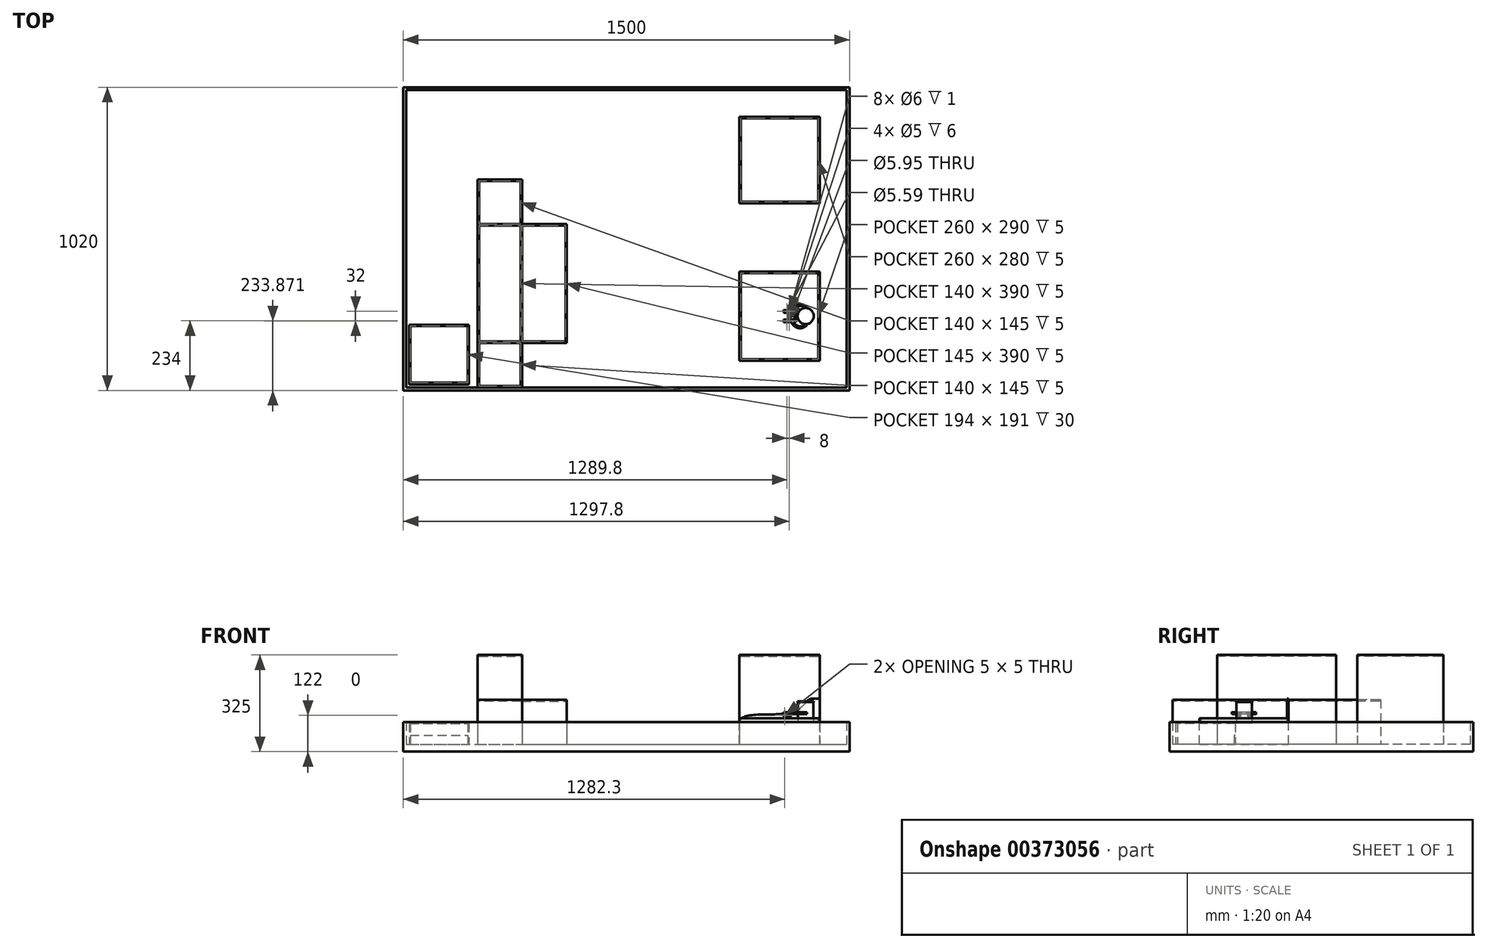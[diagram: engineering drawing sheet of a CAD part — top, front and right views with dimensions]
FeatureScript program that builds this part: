
annotation { "Feature Type Name" : "Feature", "Feature Type Description" : "" }
export const myFeature = defineFeature(function(context is Context, id is Id, definition is map)
    precondition{}
    {
        {
            var Q0;
            Q0=qCreatedBy(makeId("Top.planeOp"),FACE);
            var sketch = newSketch(context, id + "F0", { "sketchPlane" : qUnion([Q0])});
            skCircle(sketch, "E0", {"center": v(0, 0) * mm, "radius": 27.2 * mm});
            skSolve(sketch);
        }
        {
            var Q0;
            Q0=qSketchRegion(id+"F0",true);
            extrude(context, id + "F1", {"entities" : qUnion([Q0]), "depth" : 2.83 * mm});
        }
        {
            var Q0;
            Q0=makeQuery(id+"F1.opExtrude","CAP_FACE",FACE,{"disambiguationData":[OSD([sQuery(id+"F0.wireOp",EDGE,"E0")])],"isStart":false});
            var sketch = newSketch(context, id + "F2", { "sketchPlane" : qUnion([Q0])});
            skCircle(sketch, "E1", {"center": v(0, 0) * mm, "radius": 26.4 * mm});
            skSolve(sketch);
        }
        {
            var Q0;
            Q0=qSketchRegion(id+"F2",true);
            extrude(context, id + "F3", {"entities" : qUnion([Q0]), "operationType" : NewBodyOperationType.ADD, "depth" : 67.36 * mm});
        }
        {
            var Q0;
            Q0=makeQuery(id+"F3.opExtrude","CAP_FACE",FACE,{"disambiguationData":[OSD([sQuery(id+"F2.wireOp",EDGE,"E1")])],"isStart":false});
            var sketch = newSketch(context, id + "F4", { "sketchPlane" : qUnion([Q0])});
            skCircle(sketch, "E2", {"center": v(0, 0) * mm, "radius": 27.2 * mm});
            skSolve(sketch);
        }
        {
            var Q0;
            Q0=qSketchRegion(id+"F4",true);
            extrude(context, id + "F5", {"entities" : qUnion([Q0]), "operationType" : NewBodyOperationType.ADD, "depth" : 2.83 * mm});
        }
        {
            var Q0;
            Q0=makeQuery(id+"F5.opExtrude","CAP_FACE",FACE,{"disambiguationData":[OSD([sQuery(id+"F4.wireOp",EDGE,"E2")])],"isStart":false});
            var sketch = newSketch(context, id + "F6", { "sketchPlane" : qUnion([Q0])});
            skSolve(sketch);
        }
        {
            var Q0;
            Q0=qCreatedBy(makeId("Top.planeOp"),FACE);
            cPlane(context, id + "F7", {"entities" : qUnion([Q0]), "cplaneType" : CPlaneType.OFFSET, "offset" : 25 * mm, "width" : 150 * mm, "height" : 150 * mm});
        }
        {
            var Q0;
            Q0=makeQuery(id+"F6.imprint","IMPRINT",FACE,{"disambiguationData":[TD([[makeQuery(id+"F6.imprint","IMPRINT",EDGE,{"derivedFrom":makeQuery(id+"F5.opExtrude","CAP_EDGE",EDGE,{"disambiguationData":[OSD([sQuery(id+"F4.wireOp",EDGE,"E2")])],"isStart":false})}),1.0]])]});
            var sketch = newSketch(context, id + "F8", { "sketchPlane" : qUnion([Q0])});
            skSolve(sketch);
        }
        {
            var Q0;
            Q0=qCreatedBy(makeId("Top.planeOp"),FACE);
            var sketch = newSketch(context, id + "F9", { "sketchPlane" : qUnion([Q0])});
            skLineSegment(sketch, "E3.bottom", {"start": v(-222.8, -150) * mm, "end": v(47.2, -150) * mm});
            skLineSegment(sketch, "E3.top", {"start": v(-222.8, 150) * mm, "end": v(47.2, 150) * mm});
            skLineSegment(sketch, "E3.left", {"start": v(-222.8, -150) * mm, "end": v(-222.8, 150) * mm});
            skLineSegment(sketch, "E3.right", {"start": v(47.2, -150) * mm, "end": v(47.2, 150) * mm});
            skSolve(sketch);
        }
        {
            var Q0;
            Q0=qSketchRegion(id+"F9",true);
            extrude(context, id + "F10", {"entities" : qUnion([Q0]), "oppositeDirection" : true, "depth" : 72 * mm});
        }
        {
            var Q0;
            Q0=makeQuery(id+"F10.opExtrude","CAP_FACE",FACE,{"disambiguationData":[OSD([sQuery(id+"F9.wireOp",EDGE,"E3.bottom"),sQuery(id+"F9.wireOp",EDGE,"E3.top"),sQuery(id+"F9.wireOp",EDGE,"E3.left"),sQuery(id+"F9.wireOp",EDGE,"E3.right")])],"isStart":true});
            var sketch = newSketch(context, id + "F11", { "sketchPlane" : qUnion([Q0])});
            skLineSegment(sketch, "E4.bottom", {"start": v(-222.8, -150) * mm, "end": v(47.2, -150) * mm});
            skLineSegment(sketch, "E4.top", {"start": v(-222.8, -145) * mm, "end": v(42.2, -145) * mm});
            skLineSegment(sketch, "E4.left", {"start": v(-222.8, -150) * mm, "end": v(-222.8, -145) * mm});
            skLineSegment(sketch, "E5.bottom", {"start": v(47.2, 150) * mm, "end": v(42.2, 150) * mm});
            skLineSegment(sketch, "E5.left", {"start": v(47.2, 150) * mm, "end": v(47.2, -150) * mm});
            skLineSegment(sketch, "E5.right", {"start": v(42.2, 150) * mm, "end": v(42.2, -145) * mm});
            skSolve(sketch);
        }
        {
            var Q0;
            Q0=qSketchRegion(id+"F11",true);
            extrude(context, id + "F12", {"entities" : qUnion([Q0]), "operationType" : NewBodyOperationType.ADD, "depth" : 15 * mm});
        }
        {
            var Q0;
            Q0=makeQuery(id+"F12.boolean.opBoolean","MERGE",FACE,{"derivedFrom":[makeQuery(id+"F10.opExtrude","SWEPT_FACE",FACE,{"disambiguationData":[OSD([sQuery(id+"F9.wireOp",EDGE,"E3.top")])]}),makeQuery(id+"F12.opExtrude","SWEPT_FACE",FACE,{"disambiguationData":[OSD([sQuery(id+"F11.wireOp",EDGE,"E5.bottom")])]})]});
            var sketch = newSketch(context, id + "F13", { "sketchPlane" : qUnion([Q0])});
            skLineSegment(sketch, "E6", {"start": v(-47.2, 81.36) * mm, "end": v(-21.31, 81.36) * mm});
            skFitSpline(sketch, "E7", {"points": [v(-21.31, 81.36) * mm, v(15.24, 52.01) * mm, v(114.14, 28.17) * mm, v(222.8, 0) * mm], "startDerivative": vector(181.02, 0.3) * mm, "endDerivative": vector(-1.73, -239.85) * mm});
            skLineSegment(sketch, "E8", {"start": v(-47.2, 81.36) * mm, "end": v(-47.2, -72) * mm});
            skLineSegment(sketch, "E9", {"start": v(-47.2, -72) * mm, "end": v(222.8, -72) * mm});
            skLineSegment(sketch, "E10", {"start": v(222.8, -72) * mm, "end": v(222.8, 0) * mm});
            skSolve(sketch);
        }
        {
            var Q0;
            Q0=qSketchRegion(id+"F13",true);
            extrude(context, id + "F14", {"entities" : qUnion([Q0]), "operationType" : NewBodyOperationType.ADD, "oppositeDirection" : true, "depth" : 5 * mm});
        }
        {
            var Q0;
            Q0=makeQuery(id+"F10.opExtrude","CAP_FACE",FACE,{"disambiguationData":[OSD([sQuery(id+"F9.wireOp",EDGE,"E3.bottom"),sQuery(id+"F9.wireOp",EDGE,"E3.top"),sQuery(id+"F9.wireOp",EDGE,"E3.left"),sQuery(id+"F9.wireOp",EDGE,"E3.right")])],"isStart":true});
            var sketch = newSketch(context, id + "F15", { "sketchPlane" : qUnion([Q0])});
            skLineSegment(sketch, "E11.bottom", {"start": v(-222.8, 145) * mm, "end": v(-217.8, 145) * mm});
            skLineSegment(sketch, "E11.top", {"start": v(-222.8, -145) * mm, "end": v(-217.8, -145) * mm});
            skLineSegment(sketch, "E11.left", {"start": v(-222.8, 145) * mm, "end": v(-222.8, -145) * mm});
            skLineSegment(sketch, "E11.right", {"start": v(-217.8, 145) * mm, "end": v(-217.8, -145) * mm});
            skSolve(sketch);
        }
        {
            var Q0;
            Q0=qSketchRegion(id+"F15",true);
            extrude(context, id + "F16", {"entities" : qUnion([Q0]), "operationType" : NewBodyOperationType.ADD, "depth" : 5 * mm});
        }
        {
            var Q0;
            Q0=makeQuery(id+"F10.opExtrude","CAP_FACE",FACE,{"disambiguationData":[OSD([sQuery(id+"F9.wireOp",EDGE,"E3.bottom"),sQuery(id+"F9.wireOp",EDGE,"E3.top"),sQuery(id+"F9.wireOp",EDGE,"E3.left"),sQuery(id+"F9.wireOp",EDGE,"E3.right")])],"isStart":false});
            var sketch = newSketch(context, id + "F17", { "sketchPlane" : qUnion([Q0])});
            skLineSegment(sketch, "E12.bottom", {"start": v(147.2, 250) * mm, "end": v(-1352.8, 250) * mm});
            skLineSegment(sketch, "E12.top", {"start": v(147.2, -770) * mm, "end": v(-1352.8, -770) * mm});
            skLineSegment(sketch, "E12.left", {"start": v(147.2, 250) * mm, "end": v(147.2, -770) * mm});
            skLineSegment(sketch, "E12.right", {"start": v(-1352.8, 250) * mm, "end": v(-1352.8, -770) * mm});
            skSolve(sketch);
        }
        {
            var Q0;
            Q0=qSketchRegion(id+"F17",true);
            extrude(context, id + "F18", {"entities" : qUnion([Q0]), "operationType" : NewBodyOperationType.ADD, "depth" : 25 * mm});
        }
        {
            var Q0;
            Q0=makeQuery(id+"F18.opExtrude","CAP_FACE",FACE,{"disambiguationData":[OSD([sQuery(id+"F17.wireOp",EDGE,"E12.bottom"),sQuery(id+"F17.wireOp",EDGE,"E12.top"),sQuery(id+"F17.wireOp",EDGE,"E12.left"),sQuery(id+"F17.wireOp",EDGE,"E12.right")])],"isStart":true});
            var sketch = newSketch(context, id + "F19", { "sketchPlane" : qUnion([Q0])});
            skLineSegment(sketch, "E13.bottom", {"start": v(-222.8, 670) * mm, "end": v(47.2, 670) * mm});
            skLineSegment(sketch, "E13.top", {"start": v(-222.8, 380) * mm, "end": v(47.2, 380) * mm});
            skLineSegment(sketch, "E13.left", {"start": v(-222.8, 670) * mm, "end": v(-222.8, 380) * mm});
            skLineSegment(sketch, "E13.right", {"start": v(47.2, 670) * mm, "end": v(47.2, 380) * mm});
            skSolve(sketch);
        }
        {
            var Q0;
            Q0=qSketchRegion(id+"F19",true);
            extrude(context, id + "F20", {"entities" : qUnion([Q0]), "operationType" : NewBodyOperationType.ADD, "depth" : 300 * mm});
        }
        {
            var Q0;
            Q0=makeQuery(id+"F20.opExtrude","CAP_FACE",FACE,{"disambiguationData":[OSD([sQuery(id+"F19.wireOp",EDGE,"E13.bottom"),sQuery(id+"F19.wireOp",EDGE,"E13.top"),sQuery(id+"F19.wireOp",EDGE,"E13.left"),sQuery(id+"F19.wireOp",EDGE,"E13.right")])],"isStart":false});
            var sketch = newSketch(context, id + "F21", { "sketchPlane" : qUnion([Q0])});
            skLineSegment(sketch, "E14.bottom", {"start": v(-217.8, 665) * mm, "end": v(42.2, 665) * mm});
            skLineSegment(sketch, "E14.top", {"start": v(-217.8, 385) * mm, "end": v(42.2, 385) * mm});
            skLineSegment(sketch, "E14.left", {"start": v(-217.8, 665) * mm, "end": v(-217.8, 385) * mm});
            skLineSegment(sketch, "E14.right", {"start": v(42.2, 665) * mm, "end": v(42.2, 385) * mm});
            skSolve(sketch);
        }
        {
            var Q0;
            Q0=qSketchRegion(id+"F21",true);
            extrude(context, id + "F22", {"entities" : qUnion([Q0]), "operationType" : NewBodyOperationType.REMOVE, "oppositeDirection" : true, "depth" : 5 * mm});
        }
        {
            var Q0;
            Q0=makeQuery(id+"F18.opExtrude","CAP_FACE",FACE,{"disambiguationData":[OSD([sQuery(id+"F17.wireOp",EDGE,"E12.bottom"),sQuery(id+"F17.wireOp",EDGE,"E12.top"),sQuery(id+"F17.wireOp",EDGE,"E12.left"),sQuery(id+"F17.wireOp",EDGE,"E12.right")])],"isStart":true});
            var sketch = newSketch(context, id + "F23", { "sketchPlane" : qUnion([Q0])});
            skLineSegment(sketch, "E15.bottom", {"start": v(-1352.8, 770) * mm, "end": v(147.2, 770) * mm});
            skLineSegment(sketch, "E15.top", {"start": v(-1352.8, -250) * mm, "end": v(147.2, -250) * mm});
            skLineSegment(sketch, "E15.left", {"start": v(-1352.8, 770) * mm, "end": v(-1352.8, -250) * mm});
            skLineSegment(sketch, "E15.right", {"start": v(147.2, 770) * mm, "end": v(147.2, -250) * mm});
            skLineSegment(sketch, "E16.bottom", {"start": v(-1342.8, 760) * mm, "end": v(137.2, 760) * mm});
            skLineSegment(sketch, "E16.top", {"start": v(-1342.8, -240) * mm, "end": v(137.2, -240) * mm});
            skLineSegment(sketch, "E16.left", {"start": v(-1342.8, 760) * mm, "end": v(-1342.8, -240) * mm});
            skLineSegment(sketch, "E16.right", {"start": v(137.2, 760) * mm, "end": v(137.2, -240) * mm});
            skSolve(sketch);
        }
        {
            var Q0;
            Q0=qSketchRegion(id+"F23",true);
            extrude(context, id + "F24", {"entities" : qUnion([Q0]), "operationType" : NewBodyOperationType.ADD, "depth" : 75 * mm});
        }
        {
            var Q0;
            Q0=makeQuery(id+"F18.opExtrude","CAP_FACE",FACE,{"disambiguationData":[OSD([sQuery(id+"F17.wireOp",EDGE,"E12.bottom"),sQuery(id+"F17.wireOp",EDGE,"E12.top"),sQuery(id+"F17.wireOp",EDGE,"E12.left"),sQuery(id+"F17.wireOp",EDGE,"E12.right")])],"isStart":true});
            var sketch = newSketch(context, id + "F25", { "sketchPlane" : qUnion([Q0])});
            skLineSegment(sketch, "E17.bottom", {"start": v(-1102.8, 460) * mm, "end": v(-952.8, 460) * mm});
            skLineSegment(sketch, "E17.top", {"start": v(-1102.8, -240) * mm, "end": v(-952.8, -240) * mm});
            skLineSegment(sketch, "E17.left", {"start": v(-1102.8, 460) * mm, "end": v(-1102.8, -240) * mm});
            skLineSegment(sketch, "E17.right", {"start": v(-952.8, 460) * mm, "end": v(-952.8, 310) * mm});
            skLineSegment(sketch, "E18.bottom", {"start": v(-952.8, 310) * mm, "end": v(-802.8, 310) * mm});
            skLineSegment(sketch, "E18.top", {"start": v(-952.8, -90) * mm, "end": v(-802.8, -90) * mm});
            skLineSegment(sketch, "E18.right", {"start": v(-802.8, 310) * mm, "end": v(-802.8, -90) * mm});
            skLineSegment(sketch, "E19.trimOffspring", {"start": v(-952.8, -90) * mm, "end": v(-952.8, -240) * mm});
            skSolve(sketch);
        }
        {
            var Q0;
            Q0=qSketchRegion(id+"F25",true);
            extrude(context, id + "F26", {"entities" : qUnion([Q0]), "operationType" : NewBodyOperationType.ADD, "depth" : 150 * mm});
        }
        {
            var Q0;
            Q0=makeQuery(id+"F26.opExtrude","CAP_FACE",FACE,{"disambiguationData":[OSD([sQuery(id+"F25.wireOp",EDGE,"E17.bottom"),sQuery(id+"F25.wireOp",EDGE,"E17.top"),sQuery(id+"F25.wireOp",EDGE,"E17.left"),sQuery(id+"F25.wireOp",EDGE,"E17.right"),sQuery(id+"F25.wireOp",EDGE,"E18.bottom"),sQuery(id+"F25.wireOp",EDGE,"E18.top"),sQuery(id+"F25.wireOp",EDGE,"E18.right"),sQuery(id+"F25.wireOp",EDGE,"E19.trimOffspring")])],"isStart":false});
            var sketch = newSketch(context, id + "F27", { "sketchPlane" : qUnion([Q0])});
            skLineSegment(sketch, "E20.bottom", {"start": v(-952.8, 310) * mm, "end": v(-1102.8, 310) * mm});
            skLineSegment(sketch, "E20.top", {"start": v(-952.8, -90) * mm, "end": v(-1102.8, -90) * mm});
            skLineSegment(sketch, "E20.left", {"start": v(-952.8, 310) * mm, "end": v(-952.8, -90) * mm});
            skLineSegment(sketch, "E20.right", {"start": v(-1102.8, 310) * mm, "end": v(-1102.8, -90) * mm});
            skSolve(sketch);
        }
        {
            var Q0;
            Q0=qSketchRegion(id+"F27",true);
            extrude(context, id + "F28", {"entities" : qUnion([Q0]), "operationType" : NewBodyOperationType.ADD, "depth" : 150 * mm});
        }
        {
            var Q0;
            Q0=makeQuery(id+"F28.opExtrude","CAP_FACE",FACE,{"disambiguationData":[OSD([sQuery(id+"F27.wireOp",EDGE,"E20.bottom"),sQuery(id+"F27.wireOp",EDGE,"E20.top"),sQuery(id+"F27.wireOp",EDGE,"E20.left"),sQuery(id+"F27.wireOp",EDGE,"E20.right")])],"isStart":false});
            var sketch = newSketch(context, id + "F29", { "sketchPlane" : qUnion([Q0])});
            skLineSegment(sketch, "E21.bottom", {"start": v(-1097.8, 305) * mm, "end": v(-957.8, 305) * mm});
            skLineSegment(sketch, "E21.top", {"start": v(-1097.8, -85) * mm, "end": v(-957.8, -85) * mm});
            skLineSegment(sketch, "E21.left", {"start": v(-1097.8, 305) * mm, "end": v(-1097.8, -85) * mm});
            skLineSegment(sketch, "E21.right", {"start": v(-957.8, 305) * mm, "end": v(-957.8, -85) * mm});
            skSolve(sketch);
        }
        {
            var Q0;
            Q0=qSketchRegion(id+"F29",true);
            extrude(context, id + "F30", {"entities" : qUnion([Q0]), "operationType" : NewBodyOperationType.REMOVE, "oppositeDirection" : true, "depth" : 5 * mm});
        }
        {
            var Q0;
            {var subQ0=sQuery(id+"F25.wireOp",EDGE,"E17.left");var subQ1=sQuery(id+"F25.wireOp",EDGE,"E18.bottom");var subQ2=sQuery(id+"F25.wireOp",EDGE,"E17.right");var subQ3=sQuery(id+"F25.wireOp",EDGE,"E17.bottom");var subQ4=makeQuery(id+"F26.opExtrude","CAP_FACE",FACE,{"disambiguationData":[OSD([subQ3,sQuery(id+"F25.wireOp",EDGE,"E17.top"),subQ0,subQ2,subQ1,sQuery(id+"F25.wireOp",EDGE,"E18.top"),sQuery(id+"F25.wireOp",EDGE,"E18.right"),sQuery(id+"F25.wireOp",EDGE,"E19.trimOffspring")])],"isStart":false});Q0=makeQuery(id+"F28.boolean.opBoolean","SPLIT",FACE,{"disambiguationData":[TD([makeQuery(id+"F26.opExtrude","SWEPT_FACE",FACE,{"disambiguationData":[OSD([subQ3])]})])],"derivedFrom":subQ4});}
            var sketch = newSketch(context, id + "F31", { "sketchPlane" : qUnion([Q0])});
            skLineSegment(sketch, "E22.bottom", {"start": v(-1097.8, 455) * mm, "end": v(-957.8, 455) * mm});
            skLineSegment(sketch, "E22.top", {"start": v(-1097.8, 310) * mm, "end": v(-957.8, 310) * mm});
            skLineSegment(sketch, "E22.left", {"start": v(-1097.8, 455) * mm, "end": v(-1097.8, 310) * mm});
            skLineSegment(sketch, "E22.right", {"start": v(-957.8, 455) * mm, "end": v(-957.8, 310) * mm});
            skLineSegment(sketch, "E23.bottom", {"start": v(-952.8, 305) * mm, "end": v(-807.8, 305) * mm});
            skLineSegment(sketch, "E23.top", {"start": v(-952.8, -85) * mm, "end": v(-807.8, -85) * mm});
            skLineSegment(sketch, "E23.left", {"start": v(-952.8, 305) * mm, "end": v(-952.8, -85) * mm});
            skLineSegment(sketch, "E23.right", {"start": v(-807.8, 305) * mm, "end": v(-807.8, -85) * mm});
            skLineSegment(sketch, "E24.bottom", {"start": v(-1097.8, -90) * mm, "end": v(-957.8, -90) * mm});
            skLineSegment(sketch, "E24.top", {"start": v(-1097.8, -235) * mm, "end": v(-957.8, -235) * mm});
            skLineSegment(sketch, "E24.left", {"start": v(-1097.8, -90) * mm, "end": v(-1097.8, -235) * mm});
            skLineSegment(sketch, "E24.right", {"start": v(-957.8, -90) * mm, "end": v(-957.8, -235) * mm});
            skSolve(sketch);
        }
        {
            var Q0;
            Q0=qSketchRegion(id+"F31",true);
            extrude(context, id + "F32", {"entities" : qUnion([Q0]), "operationType" : NewBodyOperationType.REMOVE, "oppositeDirection" : true, "depth" : 5 * mm});
        }
        {
            var Q0;
            Q0=qCreatedBy(id+"F7.planeOp",FACE);
            var sketch = newSketch(context, id + "F33", { "sketchPlane" : qUnion([Q0])});
            skLineSegment(sketch, "E25", {"start": v(0, 0) * mm, "end": v(-90, 0) * mm, "construction": true});
            skLineSegment(sketch, "E26.bottom", {"start": v(-74.5, -12) * mm, "end": v(-55, -12) * mm});
            skLineSegment(sketch, "E26.top", {"start": v(-74.5, -20) * mm, "end": v(-55, -20) * mm});
            skLineSegment(sketch, "E26.left", {"start": v(-74.5, -12) * mm, "end": v(-74.5, -13) * mm});
            skPoint(sketch, "E27.visualSharp", {"position": v(-51, -12) * mm});
            skPoint(sketch, "E28.visualSharp", {"position": v(-51, -20) * mm});
            skCircle(sketch, "E29", {"center": v(-55, -16) * mm, "radius": 3 * mm});
            skLineSegment(sketch, "E30", {"start": v(-59, -3.98) * mm, "end": v(-59, -18.08) * mm, "construction": true});
            skCircle(sketch, "E31.MirrorC", {"center": v(-63, -16) * mm, "radius": 3 * mm});
            skLineSegment(sketch, "E32.bottom", {"start": v(-74.5, -13) * mm, "end": v(-65.65, -13) * mm});
            skLineSegment(sketch, "E32.top", {"start": v(-74.5, -19) * mm, "end": v(-65.65, -19) * mm});
            skArc(sketch, "E33", {"start": v(-65.65, -13) * mm, "mid": v(-67, -16) * mm, "end": v(-65.65, -19) * mm});
            skLineSegment(sketch, "E34.trimOffspring", {"start": v(-74.5, -19) * mm, "end": v(-74.5, -20) * mm});
            skArc(sketch, "E35.trimOffspring", {"start": v(-55, -20) * mm, "mid": v(-51, -16) * mm, "end": v(-55, -12) * mm});
            skLineSegment(sketch, "E36.MirrorCS", {"start": v(-74.5, 12) * mm, "end": v(-74.5, 13) * mm});
            skLineSegment(sketch, "E37.MirrorCS", {"start": v(-74.5, 19) * mm, "end": v(-74.5, 20) * mm});
            skPoint(sketch, "E38.MirrorP", {"position": v(-51, 12) * mm});
            skLineSegment(sketch, "E39.MirrorCS", {"start": v(-74.5, 12) * mm, "end": v(-55, 12) * mm});
            skPoint(sketch, "E40.MirrorP", {"position": v(-51, 20) * mm});
            skArc(sketch, "E41.MirrorCS", {"start": v(-65.65, 13) * mm, "mid": v(-67, 16) * mm, "end": v(-65.65, 19) * mm});
            skArc(sketch, "E42.MirrorCS", {"start": v(-55, 20) * mm, "mid": v(-51, 16) * mm, "end": v(-55, 12) * mm});
            skLineSegment(sketch, "E43.MirrorCS", {"start": v(-74.5, 20) * mm, "end": v(-55, 20) * mm});
            skCircle(sketch, "E44.MirrorC", {"center": v(-55, 16) * mm, "radius": 3 * mm});
            skCircle(sketch, "E45.MirrorC", {"center": v(-63, 16) * mm, "radius": 3 * mm});
            skLineSegment(sketch, "E46.MirrorCS", {"start": v(-74.5, 19) * mm, "end": v(-65.65, 19) * mm});
            skLineSegment(sketch, "E47.MirrorCS", {"start": v(-74.5, 13) * mm, "end": v(-65.65, 13) * mm});
            skSolve(sketch);
        }
        {
            var Q0;
            Q0=qSketchRegion(id+"F33",true);
            var Q1;
            Q1=qSketchRegion(id+"F36",true);
            extrude(context, id + "F34", {"entities" : qUnion([Q0, Q1]), "depth" : 8 * mm, "symmetric" : true});
        }
        {
            var Q0;
            Q0=makeQuery(id+"F34.opExtrude","CAP_EDGE",EDGE,{"disambiguationData":[OSD([sQuery(id+"F33.wireOp",EDGE,"E34.trimOffspring")])],"isStart":false});
            var Q1;
            Q1=makeQuery(id+"F34.opExtrude","CAP_EDGE",EDGE,{"disambiguationData":[OSD([sQuery(id+"F33.wireOp",EDGE,"E26.left")])],"isStart":false});
            var Q2;
            Q2=makeQuery(id+"F34.opExtrude","CAP_EDGE",EDGE,{"disambiguationData":[OSD([sQuery(id+"F33.wireOp",EDGE,"E34.trimOffspring")])],"isStart":true});
            var Q3;
            Q3=makeQuery(id+"F34.opExtrude","CAP_EDGE",EDGE,{"disambiguationData":[OSD([sQuery(id+"F33.wireOp",EDGE,"E26.left")])],"isStart":true});
            var Q4;
            Q4=makeQuery(id+"F34.opExtrude","CAP_EDGE",EDGE,{"disambiguationData":[OSD([sQuery(id+"F33.wireOp",EDGE,"E36.MirrorCS")])],"isStart":false});
            var Q5;
            Q5=makeQuery(id+"F34.opExtrude","CAP_EDGE",EDGE,{"disambiguationData":[OSD([sQuery(id+"F33.wireOp",EDGE,"E37.MirrorCS")])],"isStart":false});
            var Q6;
            Q6=makeQuery(id+"F34.opExtrude","CAP_EDGE",EDGE,{"disambiguationData":[OSD([sQuery(id+"F33.wireOp",EDGE,"E37.MirrorCS")])],"isStart":true});
            var Q7;
            Q7=makeQuery(id+"F34.opExtrude","CAP_EDGE",EDGE,{"disambiguationData":[OSD([sQuery(id+"F33.wireOp",EDGE,"E36.MirrorCS")])],"isStart":true});
            fillet(context, id + "F35", {"entities" : qUnion([Q0, Q1, Q2, Q3, Q4, Q5, Q6, Q7]), "radius" : 4 * mm, "tangentPropagation" : true, "allowEdgeOverflow" : false});
        }
        {
            var Q0;
            Q0=makeQuery(id+"F34.opExtrude","SWEPT_FACE",FACE,{"disambiguationData":[OSD([sQuery(id+"F33.wireOp",EDGE,"E26.top")])]});
            var sketch = newSketch(context, id + "F36", { "sketchPlane" : qUnion([Q0])});
            skCircle(sketch, "E48", {"center": v(-70.5, 25) * mm, "radius": 3 * mm});
            skSolve(sketch);
        }
        {
            var Q0;
            Q0=qSketchRegion(id+"F36",true);
            var Q1;
            Q1=makeQuery(id+"F34.opExtrude","SWEPT_FACE",FACE,{"disambiguationData":[OSD([sQuery(id+"F33.wireOp",EDGE,"E26.bottom")])]});
            extrude(context, id + "F37", {"entities" : qUnion([Q0]), "operationType" : NewBodyOperationType.ADD, "endBound" : BoundingType.UP_TO_SURFACE, "oppositeDirection" : true, "endBoundEntityFace" : qUnion([Q1]), "depth" : 25 * mm});
        }
        {
            var Q0;
            Q0=makeQuery(id+"F34.opExtrude","SWEPT_FACE",FACE,{"disambiguationData":[OSD([sQuery(id+"F33.wireOp",EDGE,"E43.MirrorCS")])]});
            var sketch = newSketch(context, id + "F38", { "sketchPlane" : qUnion([Q0])});
            skCircle(sketch, "E49", {"center": v(70.5, 25) * mm, "radius": 3 * mm});
            skSolve(sketch);
        }
        {
            var Q0;
            Q0=qSketchRegion(id+"F38",true);
            var Q1;
            Q1=makeQuery(id+"F34.opExtrude","SWEPT_FACE",FACE,{"disambiguationData":[OSD([sQuery(id+"F33.wireOp",EDGE,"E39.MirrorCS")])]});
            extrude(context, id + "F39", {"entities" : qUnion([Q0]), "operationType" : NewBodyOperationType.ADD, "endBound" : BoundingType.UP_TO_SURFACE, "oppositeDirection" : true, "endBoundEntityFace" : qUnion([Q1]), "depth" : 25 * mm});
        }
        {
            var Q0;
            Q0=qCreatedBy(id+"F7.planeOp",FACE);
            var sketch = newSketch(context, id + "F40", { "sketchPlane" : qUnion([Q0])});
            skCircle(sketch, "E50", {"center": v(-55, 16) * mm, "radius": 3 * mm});
            skCircle(sketch, "E51", {"center": v(-63, 16) * mm, "radius": 2.5 * mm});
            skCircle(sketch, "E52", {"center": v(-63, 16) * mm, "radius": 3 * mm});
            skCircle(sketch, "E53", {"center": v(-55, 16) * mm, "radius": 2.5 * mm});
            skSolve(sketch);
        }
        {
            var Q0;
            Q0=qSketchRegion(id+"F40",true);
            extrude(context, id + "F41", {"entities" : qUnion([Q0]), "operationType" : NewBodyOperationType.ADD, "depth" : 6 * mm, "symmetric" : true});
        }
        {
            var Q0;
            Q0=qCreatedBy(id+"F7.planeOp",FACE);
            var sketch = newSketch(context, id + "F42", { "sketchPlane" : qUnion([Q0])});
            skCircle(sketch, "E54", {"center": v(-63, -16) * mm, "radius": 2.5 * mm});
            skCircle(sketch, "E55", {"center": v(-63, -16) * mm, "radius": 3 * mm});
            skCircle(sketch, "E56", {"center": v(-55, -16) * mm, "radius": 2.5 * mm});
            skCircle(sketch, "E57", {"center": v(-55, -16) * mm, "radius": 3 * mm});
            skSolve(sketch);
        }
        {
            var Q0;
            Q0=qSketchRegion(id+"F42",true);
            extrude(context, id + "F43", {"entities" : qUnion([Q0]), "operationType" : NewBodyOperationType.ADD, "depth" : 6 * mm, "symmetric" : true});
        }
        {
            var Q0;
            Q0=makeQuery(id+"F34.opExtrude","SWEPT_FACE",FACE,{"disambiguationData":[OSD([sQuery(id+"F33.wireOp",EDGE,"E43.MirrorCS")])]});
            var sketch = newSketch(context, id + "F44", { "sketchPlane" : qUnion([Q0])});
            skArc(sketch, "E58", {"start": v(71.5, 27.3) * mm, "mid": v(70.5, 27.5) * mm, "end": v(69.5, 27.3) * mm});
            skLineSegment(sketch, "E59.bottom", {"start": v(68.2, 26) * mm, "end": v(69.5, 26) * mm});
            skLineSegment(sketch, "E59.top", {"start": v(68.2, 24) * mm, "end": v(69.5, 24) * mm});
            skLineSegment(sketch, "E60.left", {"start": v(71.5, 27.3) * mm, "end": v(71.5, 26) * mm});
            skLineSegment(sketch, "E60.right", {"start": v(69.5, 27.3) * mm, "end": v(69.5, 26) * mm});
            skPoint(sketch, "E61.orphan", {"position": v(69.5, 27.8) * mm});
            skPoint(sketch, "E62.orphan", {"position": v(71.5, 27.8) * mm});
            skArc(sketch, "E63.trimOffspring", {"start": v(68.2, 26) * mm, "mid": v(68, 25) * mm, "end": v(68.2, 24) * mm});
            skPoint(sketch, "E59.left.start.orphan", {"position": v(67.32, 26) * mm});
            skPoint(sketch, "E64.orphan", {"position": v(67.32, 24) * mm});
            skArc(sketch, "E65.trimOffspring", {"start": v(69.5, 22.7) * mm, "mid": v(70.5, 22.5) * mm, "end": v(71.5, 22.7) * mm});
            skLineSegment(sketch, "E66.trimOffspring", {"start": v(69.5, 24) * mm, "end": v(69.5, 22.7) * mm});
            skLineSegment(sketch, "E67.trimOffspring", {"start": v(71.5, 26) * mm, "end": v(72.8, 26) * mm});
            skLineSegment(sketch, "E68.trimOffspring", {"start": v(71.5, 24) * mm, "end": v(71.5, 22.7) * mm});
            skLineSegment(sketch, "E69.trimOffspring", {"start": v(71.5, 24) * mm, "end": v(72.8, 24) * mm});
            skPoint(sketch, "E60.top.end.orphan", {"position": v(69.5, 22.2) * mm});
            skPoint(sketch, "E70.orphan", {"position": v(71.5, 22.2) * mm});
            skPoint(sketch, "E59.right.end.orphan", {"position": v(73.68, 24) * mm});
            skPoint(sketch, "E71.orphan", {"position": v(73.68, 26) * mm});
            skArc(sketch, "E72.trimOffspring", {"start": v(72.8, 24) * mm, "mid": v(73, 25) * mm, "end": v(72.8, 26) * mm});
            skSolve(sketch);
        }
        {
            var Q0;
            Q0=qSketchRegion(id+"F44",true);
            extrude(context, id + "F45", {"entities" : qUnion([Q0]), "operationType" : NewBodyOperationType.REMOVE, "endBound" : BoundingType.THROUGH_ALL, "oppositeDirection" : true, "depth" : 25 * mm});
        }
        {
            var Q0;
            Q0=makeQuery(id+"F18.opExtrude","CAP_FACE",FACE,{"disambiguationData":[OSD([sQuery(id+"F17.wireOp",EDGE,"E12.bottom"),sQuery(id+"F17.wireOp",EDGE,"E12.top"),sQuery(id+"F17.wireOp",EDGE,"E12.left"),sQuery(id+"F17.wireOp",EDGE,"E12.right")])],"isStart":true});
            var sketch = newSketch(context, id + "F46", { "sketchPlane" : qUnion([Q0])});
            skLineSegment(sketch, "E73.bottom", {"start": v(-1332.8, -30) * mm, "end": v(-1132.8, -30) * mm});
            skLineSegment(sketch, "E73.top", {"start": v(-1332.8, -230) * mm, "end": v(-1132.8, -230) * mm});
            skLineSegment(sketch, "E73.left", {"start": v(-1332.8, -30) * mm, "end": v(-1332.8, -230) * mm});
            skLineSegment(sketch, "E73.right", {"start": v(-1132.8, -30) * mm, "end": v(-1132.8, -230) * mm});
            skLineSegment(sketch, "E74.bottom", {"start": v(-1329.8, -33) * mm, "end": v(-1135.8, -33) * mm});
            skLineSegment(sketch, "E74.top", {"start": v(-1329.8, -224) * mm, "end": v(-1135.8, -224) * mm});
            skLineSegment(sketch, "E74.left", {"start": v(-1329.8, -33) * mm, "end": v(-1329.8, -224) * mm});
            skLineSegment(sketch, "E74.right", {"start": v(-1135.8, -33) * mm, "end": v(-1135.8, -224) * mm});
            skSolve(sketch);
        }
        {
            var Q0;
            Q0=qSketchRegion(id+"F46",true);
            extrude(context, id + "F47", {"entities" : qUnion([Q0]), "operationType" : NewBodyOperationType.ADD, "depth" : 30 * mm});
        }
        {
            var Q0;
            Q0=makeQuery(id+"F47.opExtrude","CAP_FACE",FACE,{"disambiguationData":[OSD([sQuery(id+"F46.wireOp",EDGE,"E73.bottom"),sQuery(id+"F46.wireOp",EDGE,"E73.top"),sQuery(id+"F46.wireOp",EDGE,"E73.left"),sQuery(id+"F46.wireOp",EDGE,"E73.right"),sQuery(id+"F46.wireOp",EDGE,"E74.bottom"),sQuery(id+"F46.wireOp",EDGE,"E74.top"),sQuery(id+"F46.wireOp",EDGE,"E74.left"),sQuery(id+"F46.wireOp",EDGE,"E74.right")])],"isStart":false});
            var sketch = newSketch(context, id + "F48", { "sketchPlane" : qUnion([Q0])});
            skLineSegment(sketch, "E75.bottom", {"start": v(-1332.8, -30) * mm, "end": v(-1329.8, -30) * mm});
            skLineSegment(sketch, "E75.top", {"start": v(-1332.8, -230) * mm, "end": v(-1329.8, -230) * mm});
            skLineSegment(sketch, "E75.left", {"start": v(-1332.8, -30) * mm, "end": v(-1332.8, -230) * mm});
            skLineSegment(sketch, "E75.right", {"start": v(-1329.8, -30) * mm, "end": v(-1329.8, -224) * mm});
            skLineSegment(sketch, "E76.bottom", {"start": v(-1329.8, -230) * mm, "end": v(-1135.8, -230) * mm});
            skLineSegment(sketch, "E76.top", {"start": v(-1329.8, -224) * mm, "end": v(-1135.8, -224) * mm});
            skLineSegment(sketch, "E77.bottom", {"start": v(-1135.8, -230) * mm, "end": v(-1132.8, -230) * mm});
            skLineSegment(sketch, "E77.top", {"start": v(-1135.8, -30) * mm, "end": v(-1132.8, -30) * mm});
            skLineSegment(sketch, "E77.left", {"start": v(-1135.8, -224) * mm, "end": v(-1135.8, -30) * mm});
            skLineSegment(sketch, "E77.right", {"start": v(-1132.8, -230) * mm, "end": v(-1132.8, -30) * mm});
            skSolve(sketch);
        }
        {
            var Q0;
            Q0=qSketchRegion(id+"F48",true);
            extrude(context, id + "F49", {"entities" : qUnion([Q0]), "operationType" : NewBodyOperationType.ADD, "depth" : 40 * mm});
        }
        {
            var Q0;
            Q0=makeQuery(id+"F34.opExtrude","CAP_FACE",FACE,{"disambiguationData":[OSD([sQuery(id+"F33.wireOp",EDGE,"E36.MirrorCS"),sQuery(id+"F33.wireOp",EDGE,"E37.MirrorCS"),sQuery(id+"F33.wireOp",EDGE,"E39.MirrorCS"),sQuery(id+"F33.wireOp",EDGE,"E41.MirrorCS"),sQuery(id+"F33.wireOp",EDGE,"E42.MirrorCS"),sQuery(id+"F33.wireOp",EDGE,"E43.MirrorCS"),sQuery(id+"F33.wireOp",EDGE,"E44.MirrorC"),sQuery(id+"F33.wireOp",EDGE,"E45.MirrorC"),sQuery(id+"F33.wireOp",EDGE,"E46.MirrorCS"),sQuery(id+"F33.wireOp",EDGE,"E47.MirrorCS")])],"isStart":false});
            var sketch = newSketch(context, id + "F50", { "sketchPlane" : qUnion([Q0])});
            skPoint(sketch, "E78.middle", {"position": v(0.1, -0.42) * mm});
            skLineSegment(sketch, "E79", {"start": v(-39.83, -18.9) * mm, "end": v(-29.29, -15.06) * mm});
            skLineSegment(sketch, "E80", {"start": v(-39.83, 15.63) * mm, "end": v(-29.29, 11.8) * mm});
            skLineSegment(sketch, "E81", {"start": v(-2.4, 30.2) * mm, "end": v(3.9, 30.2) * mm});
            skLineSegment(sketch, "E82", {"start": v(-2.4, -30.2) * mm, "end": v(3.9, -30.2) * mm});
            skArc(sketch, "E83", {"start": v(-39.83, -18.9) * mm, "mid": v(-23.84, -33.55) * mm, "end": v(-2.4, -30.2) * mm});
            skArc(sketch, "E84", {"start": v(-2.4, 30.2) * mm, "mid": v(-24.78, 32.34) * mm, "end": v(-39.83, 15.63) * mm});
            skLineSegment(sketch, "E85", {"start": v(-73.77, 20.73) * mm, "end": v(-46.5, 20.73) * mm});
            skLineSegment(sketch, "E86", {"start": v(-46.5, 11.8) * mm, "end": v(-35.22, 7.7) * mm});
            skLineSegment(sketch, "E87", {"start": v(-46.5, 11.8) * mm, "end": v(-73.81, 11.8) * mm});
            skLineSegment(sketch, "E88", {"start": v(-73.81, 11.8) * mm, "end": v(-73.77, 20.73) * mm});
            skArc(sketch, "E89", {"start": v(3.9, 30.2) * mm, "mid": v(-23.96, 39.63) * mm, "end": v(-46.5, 20.73) * mm});
            skLineSegment(sketch, "E90", {"start": v(-74.54, -11.35) * mm, "end": v(-74.54, -20.58) * mm});
            skLineSegment(sketch, "E91", {"start": v(-74.54, -20.58) * mm, "end": v(-47.06, -20.58) * mm});
            skArc(sketch, "E92", {"start": v(-29.29, 11.8) * mm, "mid": v(-32.29, -1.63) * mm, "end": v(-29.29, -15.06) * mm});
            skArc(sketch, "E93", {"start": v(-35.22, 7.7) * mm, "mid": v(-37.64, -0.77) * mm, "end": v(-35.22, -9.22) * mm});
            skCircle(sketch, "E94", {"center": v(-63, 16) * mm, "radius": 2.8 * mm});
            skCircle(sketch, "E95", {"center": v(-55, 16) * mm, "radius": 2.72 * mm});
            skCircle(sketch, "E96", {"center": v(-55, -16.13) * mm, "radius": 2.98 * mm});
            skCircle(sketch, "E97", {"center": v(-63, -16) * mm, "radius": 2.56 * mm});
            skLineSegment(sketch, "E98", {"start": v(-46.5, -11.35) * mm, "end": v(-35.22, -9.22) * mm});
            skLineSegment(sketch, "E99", {"start": v(-74.54, -11.35) * mm, "end": v(-46.5, -11.35) * mm});
            skArc(sketch, "E100", {"start": v(-47.06, -20.58) * mm, "mid": v(-24.43, -40.46) * mm, "end": v(3.9, -30.2) * mm});
            skSolve(sketch);
        }
        {
            var Q0;
            Q0 = qSketchRegion(id + "F50", true);
            extrude(context, id + "F51", {"entities" : qUnion([Q0]), "depth" : 6 * mm});
        }
    });
